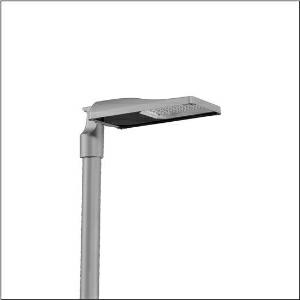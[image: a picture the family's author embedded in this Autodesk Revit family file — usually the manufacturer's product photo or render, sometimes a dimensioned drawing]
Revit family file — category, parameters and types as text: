
# Revit family: streetlight_sl_31_mini___st1_0a_5xh2d31a08ga_4fc3
name_source: partatom
category: Lighting Fixtures
units: mm (PartAtom-declared; Revit-internal decimal feet)

## family parameters
Cut with Voids When Loaded = No
Host = Face
Light Source = No
Part Type = Normal
Room Calculation Point = No
Round Connector Dimension = Use Diameter
Shared = No

## types (1)
- --- (1 x LED, 5710 lm, 37.3 W, 3000K)
    Apparent Load = 37 VA
    CIE Flux Codes = 37 72 97 100 100
    Color Rendering = 70
    Color Temperature = 3000K
    Default Elevation = 1800 mm
    Description = Streetlight SL 31 mini Easy, Desk-Remote mast luminaire for post-top, side-entry; light control with lens of PMMA; light distribution: ST1.0a, direct asymmetric distribution, for standard-compliant lighting for roads and squares; LED: luminous flux: 5.710lm, light colour: 730, colour temperature: 3000K; luminous efficacy: 153,1lm/W; control: pre-setting: linear dimming characteristic, flexible luminous flux parameterisation, time-dependent luminous flux control, constant luminous flux control, intelligent temperature release in ECG and LED module, overheat protection; luminaire housing, of diecast aluminium, SITECO metallic grey (DB 702S), corrosivity category C5 high according to DIN EN ISO 12944; cover of toughened safety glass, transparent, mast flange of diecast aluminium, SITECO metallic grey (DB 702S), spigot size: 76/60mm, mast flange included unmounted; with cable H07RN-F 2x 1.5mm², cable length: 6,5m, connection cable pre-assembled; mains connection: 220..240V, AC, 50/60Hz; power consumption (at start of service life): 37,3W / (at end of service life): 38,7W / (with reduced operation 50%): 17,5W; protection rating (complete): IP66; insulation class (complete): insulation class II (safety insulation); impact resistance: IK10; certification: CE, ENEC, ENEC+, VDE, UKCA; permissible operating ambient temperature for outdoor applications: -40..+50°C; packaging unit: 1 piece

Light Distribution: ST1.0a
    Height = 76 mm
    Lamp = 1 x LED
    Lamp Light Flux = 5710 lm
    Lamp Power = 37.3 W
    Lamp count = 1
    Length = 547 mm
    Luminous efficacy = 153 lm/W
    Manufacturer = Siteco
    ModVariant = No
    Model = 5XH2D31A08GA
    Number of Poles = 1
    OnlyDefault = Yes
    Power Factor = 1
    Product Name = Streetlight SL 31 mini | ST1.0a
    Product group = mast luminaire | pylon top
    ProductGroupID = 6100
    Protection Class = Protection class II
    Protection Degree = IP 66
    RLX_Detail_Level = 1
    RLX_Emergency_Light_Flux = 0 lm
    RLX_Emergency_Type = 0
    RLX_Emergency_Type_DB = No
    RlxData = <blob elided: 39477 chars, md5=1549fb57>
    Socket = socket
    Standby Power = 0 W
    System Light Flux = 5710 lm
    System Power = 37 W
    Type Comments = factory setting: luminous flux: 100 % | dim-lin: 254 | 386 mA
    Type Image = l_1300326.jpg
    URL = http://relux.com
    VarID = @adj_061885
    Voltage = 0 V
    Weight = 0.00 kg
    Width = 265 mm

## geometry (parser evidence)
native form markers: Blend x4, Sweep x11
no freeform markers — native parametric forms only
